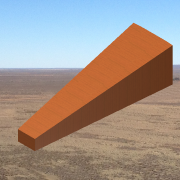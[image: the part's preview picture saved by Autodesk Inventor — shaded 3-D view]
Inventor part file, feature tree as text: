
AUTODESK INVENTOR PART (.ipt)
format: ipt  version: 2014 SP1 (Build 180222100, 222)  size: 141,824 bytes
history: native  units: in
note: dims shown in document units (in); Inventor stores cm internally (conversion verified against a paired STEP export)
features: sketch x3, revolve x2, extrude x1
ambient origin geometry x8: Origin, YZ Plane, XZ Plane, XY Plane, X Axis, Y Axis, Z Axis, Center Point
bodies: Solid1 (feature_tree)
feature tree (6):
  extrude  "Extrusion1"  Depth=16.0in
  revolve  "Revolution1"  [1 undecoded]
  revolve  "Revolution2"  [1 undecoded]
  sketch  "Sketch1"  dims[d0=60.0in d1=16.0in]
  sketch  "Sketch2"  dims[d2=5.0in d3=8.0in d4=0.0in]
  sketch  "Sketch3"  dims[d5=0.0344in d6=0.0344in]
note: 2 required parameter values undecoded (feature->parameter linkage not recoverable at this tier; creation-order binding heuristic only, values carry confidence <= 0.55)
